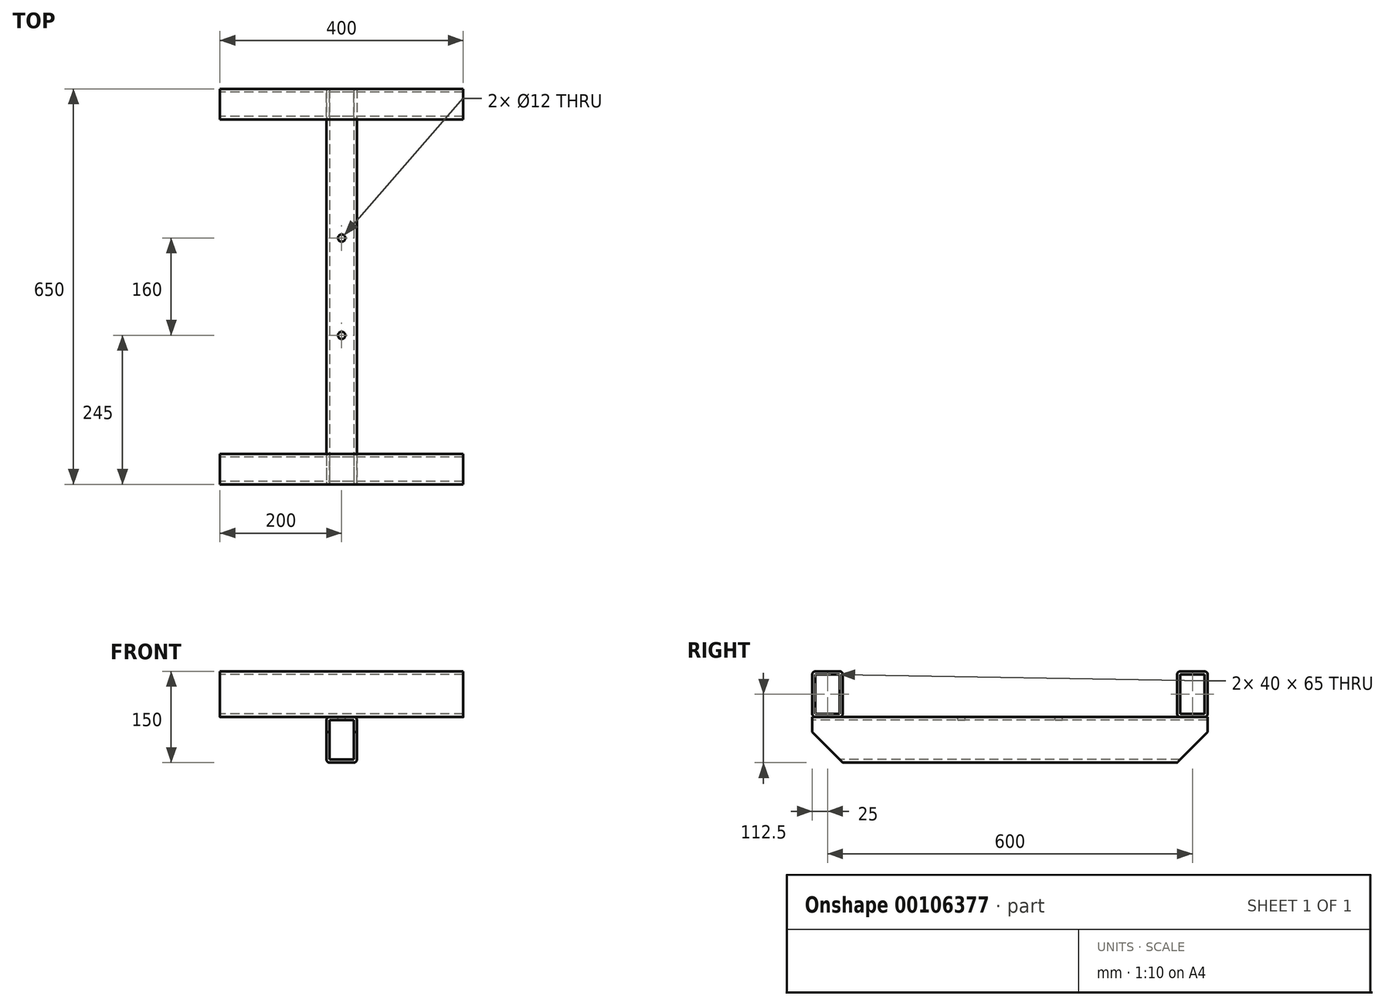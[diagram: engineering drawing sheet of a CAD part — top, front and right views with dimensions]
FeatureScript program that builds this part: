
annotation { "Feature Type Name" : "Feature", "Feature Type Description" : "" }
export const myFeature = defineFeature(function(context is Context, id is Id, definition is map)
    precondition{}
    {
        {
            var Q0;
            Q0=qCreatedBy(makeId("Front.planeOp"),FACE);
            var sketch = newSketch(context, id + "F0", { "sketchPlane" : qUnion([Q0])});
            skLineSegment(sketch, "E0.bottom", {"start": v(20, -37.5) * mm, "end": v(-20, -37.5) * mm});
            skLineSegment(sketch, "E0.top", {"start": v(20, 37.5) * mm, "end": v(-20, 37.5) * mm});
            skLineSegment(sketch, "E0.left", {"start": v(25, -32.5) * mm, "end": v(25, 32.5) * mm});
            skLineSegment(sketch, "E0.right", {"start": v(-25, -32.5) * mm, "end": v(-25, 32.5) * mm});
            skPoint(sketch, "E0.middle", {"position": v(0, 0) * mm});
            skPoint(sketch, "E1.visualSharp", {"position": v(-25, 37.5) * mm});
            skArc(sketch, "E1.filletArc", {"start": v(-20, 37.5) * mm, "mid": v(-23.54, 36.04) * mm, "end": v(-25, 32.5) * mm});
            skPoint(sketch, "E2.visualSharp", {"position": v(25, 37.5) * mm});
            skArc(sketch, "E2.filletArc", {"start": v(25, 32.5) * mm, "mid": v(23.54, 36.04) * mm, "end": v(20, 37.5) * mm});
            skPoint(sketch, "E3.visualSharp", {"position": v(25, -37.5) * mm});
            skArc(sketch, "E3.filletArc", {"start": v(20, -37.5) * mm, "mid": v(23.54, -36.04) * mm, "end": v(25, -32.5) * mm});
            skPoint(sketch, "E4.visualSharp", {"position": v(-25, -37.5) * mm});
            skArc(sketch, "E4.filletArc", {"start": v(-25, -32.5) * mm, "mid": v(-23.54, -36.04) * mm, "end": v(-20, -37.5) * mm});
            skLineSegment(sketch, "E5.0", {"start": v(-20, -32.5) * mm, "end": v(-20, 32.5) * mm});
            skLineSegment(sketch, "E5.1", {"start": v(20, -32.5) * mm, "end": v(-20, -32.5) * mm});
            skLineSegment(sketch, "E5.2", {"start": v(20, -32.5) * mm, "end": v(20, 32.5) * mm});
            skLineSegment(sketch, "E5.3", {"start": v(20, 32.5) * mm, "end": v(-20, 32.5) * mm});
            skSolve(sketch);
        }
        {
            var Q0;
            Q0 = qSketchRegion(id + "F0", true);
            extrude(context, id + "F1", {"entities" : qUnion([Q0]), "oppositeDirection" : true, "depth" : 650 * mm});
        }
        {
            var Q0;
            Q0=makeQuery(id+"F1.opExtrude","SWEPT_FACE",FACE,{"disambiguationData":[OSD([sQuery(id+"F0.wireOp",EDGE,"E0.top")])]});
            var sketch = newSketch(context, id + "F2", { "sketchPlane" : qUnion([Q0])});
            skPoint(sketch, "E6", {"position": v(0, 0) * mm});
            skLineSegment(sketch, "E7", {"start": v(-20, 325) * mm, "end": v(20, 325) * mm, "construction": true});
            skLineSegment(sketch, "E8", {"start": v(0, 325) * mm, "end": v(0, 245) * mm, "construction": true});
            skLineSegment(sketch, "E9", {"start": v(0, 325) * mm, "end": v(0, 405) * mm, "construction": true});
            skCircle(sketch, "E10", {"center": v(0, 245) * mm, "radius": 6 * mm});
            skCircle(sketch, "E11", {"center": v(0, 405) * mm, "radius": 6 * mm});
            skSolve(sketch);
        }
        {
            var Q0;
            Q0 = qSketchRegion(id + "F2", true);
            extrude(context, id + "F3", {"entities" : qUnion([Q0]), "operationType" : NewBodyOperationType.REMOVE, "endBound" : BoundingType.UP_TO_NEXT, "oppositeDirection" : true, "depth" : 25 * mm});
        }
        {
            var Q0;
            Q0=makeQuery(id+"F1.opExtrude","SWEPT_FACE",FACE,{"disambiguationData":[OSD([sQuery(id+"F0.wireOp",EDGE,"E0.top")])]});
            var sketch = newSketch(context, id + "F4", { "sketchPlane" : qUnion([Q0])});
            skLineSegment(sketch, "E12.bottom", {"start": v(200, 0) * mm, "end": v(-200, 0) * mm, "construction": true});
            skLineSegment(sketch, "E12.top", {"start": v(200, 50) * mm, "end": v(-200, 50) * mm, "construction": true});
            skLineSegment(sketch, "E12.left", {"start": v(200, 0) * mm, "end": v(200, 50) * mm, "construction": true});
            skLineSegment(sketch, "E12.right", {"start": v(-200, 0) * mm, "end": v(-200, 50) * mm, "construction": true});
            skPoint(sketch, "E12.middle", {"position": v(0, 25) * mm});
            skLineSegment(sketch, "E13", {"start": v(0, 50) * mm, "end": v(0, 0) * mm, "construction": true});
            skLineSegment(sketch, "E14", {"start": v(-20, 325) * mm, "end": v(20, 325) * mm, "construction": true});
            skSolve(sketch);
        }
        {
            var Q0;
            Q0=qCreatedBy(makeId("Right.planeOp"),FACE);
            var sketch = newSketch(context, id + "F5", { "sketchPlane" : qUnion([Q0])});
            skLineSegment(sketch, "E15.bottom", {"start": v(5, 37.5) * mm, "end": v(45, 37.5) * mm});
            skLineSegment(sketch, "E15.top", {"start": v(5, 112.5) * mm, "end": v(45, 112.5) * mm});
            skLineSegment(sketch, "E15.left", {"start": v(0, 42.5) * mm, "end": v(0, 107.5) * mm});
            skLineSegment(sketch, "E15.right", {"start": v(50, 42.5) * mm, "end": v(50, 107.5) * mm});
            skPoint(sketch, "E16.visualSharp", {"position": v(50, 112.5) * mm});
            skArc(sketch, "E16.filletArc", {"start": v(50, 107.5) * mm, "mid": v(48.54, 111.04) * mm, "end": v(45, 112.5) * mm});
            skPoint(sketch, "E17.visualSharp", {"position": v(0, 37.5) * mm});
            skArc(sketch, "E17.filletArc", {"start": v(0, 42.5) * mm, "mid": v(1.46, 38.96) * mm, "end": v(5, 37.5) * mm});
            skPoint(sketch, "E18.visualSharp", {"position": v(50, 37.5) * mm});
            skArc(sketch, "E18.filletArc", {"start": v(45, 37.5) * mm, "mid": v(48.54, 38.96) * mm, "end": v(50, 42.5) * mm});
            skPoint(sketch, "E19.visualSharp", {"position": v(0, 112.5) * mm});
            skArc(sketch, "E19.filletArc", {"start": v(5, 112.5) * mm, "mid": v(1.46, 111.04) * mm, "end": v(0, 107.5) * mm});
            skLineSegment(sketch, "E20.0", {"start": v(5, 42.5) * mm, "end": v(5, 107.5) * mm});
            skLineSegment(sketch, "E20.1", {"start": v(5, 42.5) * mm, "end": v(45, 42.5) * mm});
            skLineSegment(sketch, "E20.2", {"start": v(45, 42.5) * mm, "end": v(45, 107.5) * mm});
            skLineSegment(sketch, "E20.3", {"start": v(5, 107.5) * mm, "end": v(45, 107.5) * mm});
            skSolve(sketch);
        }
        {
            var Q0;
            Q0 = qSketchRegion(id + "F5", true);
            extrude(context, id + "F6", {"entities" : qUnion([Q0]), "operationType" : NewBodyOperationType.ADD, "endBound" : BoundingType.SYMMETRIC, "depth" : 400 * mm});
        }
        {
            var Q0;
            Q0=sQuery(id+"F4.wireOp",VERTEX,"E14.start");
            var Q1;
            Q1=makeQuery(id+"F1.opExtrude","CAP_FACE",FACE,{"disambiguationData":[OSD([sQuery(id+"F0.wireOp",EDGE,"E0.bottom"),sQuery(id+"F0.wireOp",EDGE,"E0.top"),sQuery(id+"F0.wireOp",EDGE,"E0.left"),sQuery(id+"F0.wireOp",EDGE,"E0.right"),sQuery(id+"F0.wireOp",EDGE,"E1.filletArc"),sQuery(id+"F0.wireOp",EDGE,"E2.filletArc"),sQuery(id+"F0.wireOp",EDGE,"E3.filletArc"),sQuery(id+"F0.wireOp",EDGE,"E4.filletArc"),sQuery(id+"F0.wireOp",EDGE,"E5.0"),sQuery(id+"F0.wireOp",EDGE,"E5.1"),sQuery(id+"F0.wireOp",EDGE,"E5.2"),sQuery(id+"F0.wireOp",EDGE,"E5.3")])],"isStart":true});
            cPlane(context, id + "F7", {"entities" : qUnion([Q0, Q1]), "cplaneType" : CPlaneType.PLANE_POINT, "offset" : 25 * mm, "width" : 150 * mm, "height" : 150 * mm});
        }
        {
            var Q0;
            Q0=makeQuery(id+"F1.opExtrude","SWEPT_BODY",BODY,{"disambiguationData":[OSD([sQuery(id+"F0.wireOp",EDGE,"E0.bottom"),sQuery(id+"F0.wireOp",EDGE,"E0.top"),sQuery(id+"F0.wireOp",EDGE,"E0.left"),sQuery(id+"F0.wireOp",EDGE,"E0.right"),sQuery(id+"F0.wireOp",EDGE,"E1.filletArc"),sQuery(id+"F0.wireOp",EDGE,"E2.filletArc"),sQuery(id+"F0.wireOp",EDGE,"E3.filletArc"),sQuery(id+"F0.wireOp",EDGE,"E4.filletArc"),sQuery(id+"F0.wireOp",EDGE,"E5.0"),sQuery(id+"F0.wireOp",EDGE,"E5.1"),sQuery(id+"F0.wireOp",EDGE,"E5.2"),sQuery(id+"F0.wireOp",EDGE,"E5.3")])]});
            var Q1;
            Q1=qCreatedBy(id+"F7.planeOp",FACE);
            mirror(context, id + "F8", {"operationType" : NewBodyOperationType.ADD, "entities" : qUnion([Q0]), "mirrorPlane" : qUnion([Q1])});
        }
        {
            var Q0;
            Q0=makeQuery(id+"F1.opExtrude","CAP_EDGE",EDGE,{"disambiguationData":[OSD([sQuery(id+"F0.wireOp",EDGE,"E0.bottom")])],"isStart":true});
            chamfer(context, id + "F9", {"entities" : qUnion([Q0]), "width" : 50 * mm});
        }
        {
            var Q0;
            Q0=makeQuery(id+"F1.opExtrude","CAP_EDGE",EDGE,{"disambiguationData":[OSD([sQuery(id+"F0.wireOp",EDGE,"E0.bottom")])],"isStart":false});
            chamfer(context, id + "F10", {"entities" : qUnion([Q0]), "width" : 50 * mm});
        }
    });
